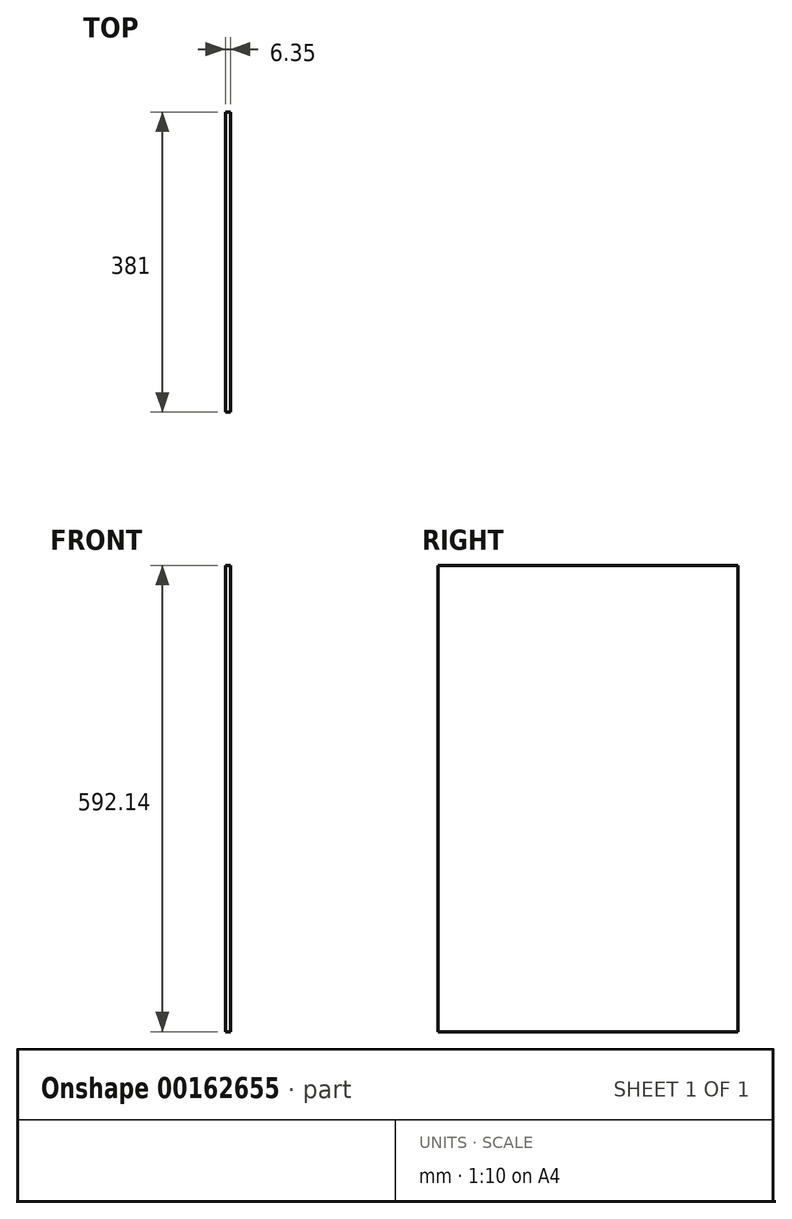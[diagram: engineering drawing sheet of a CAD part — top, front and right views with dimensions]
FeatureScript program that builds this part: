
annotation { "Feature Type Name" : "Feature", "Feature Type Description" : "" }
export const myFeature = defineFeature(function(context is Context, id is Id, definition is map)
    precondition{}
    {
        {
            var Q0;
            Q0=qCreatedBy(makeId("Right.planeOp"),FACE);
            var sketch = newSketch(context, id + "F0", { "sketchPlane" : qUnion([Q0])});
            skLineSegment(sketch, "E0.bottom", {"start": v(-208.02, 329.06) * mm, "end": v(172.98, 329.06) * mm});
            skLineSegment(sketch, "E0.top", {"start": v(-208.02, -263.08) * mm, "end": v(172.98, -263.08) * mm});
            skLineSegment(sketch, "E0.left", {"start": v(-208.02, 329.06) * mm, "end": v(-208.02, -263.08) * mm});
            skLineSegment(sketch, "E0.right", {"start": v(172.98, 329.06) * mm, "end": v(172.98, -263.08) * mm});
            skSolve(sketch);
        }
        {
            var Q0;
            Q0 = qSketchRegion(id + "F0", true);
            extrude(context, id + "F1", {"entities" : qUnion([Q0]), "depth" : 6.35 * mm});
        }
    });
